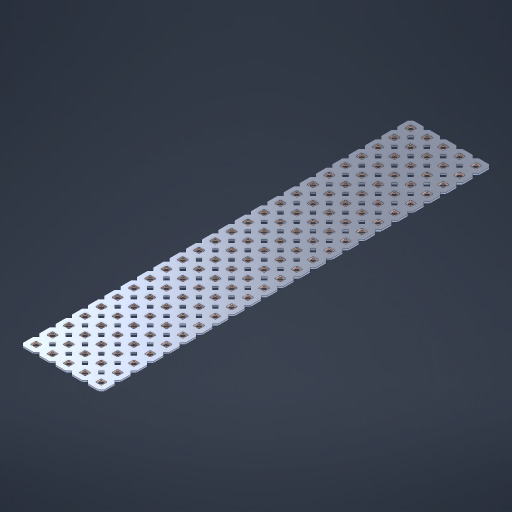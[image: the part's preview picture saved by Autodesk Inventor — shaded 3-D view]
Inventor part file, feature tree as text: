
AUTODESK INVENTOR PART (.ipt)
format: ipt  version: 2023 (Build 270158000, 158)  size: 1,647,616 bytes
history: native  units: in
note: dims shown in document units (in); Inventor stores cm internally (conversion verified against a paired STEP export)
features: other x121, extrude x119, sketch x2, pattern_linear x1
ambient origin geometry x8: Origin, YZ Plane, XZ Plane, XY Plane, X Axis, Y Axis, Z Axis, Center Point
bodies: Solid1 (feature_tree), Body (feature_tree)
feature tree (243):
  pattern_linear  "Rectangular Pattern1"  Spacing1=0.09in  [1 undecoded]
  sketch  "Sketch1"  dims[d1=0.5in]
  sketch  "Sketch2"  dims[d2=0.182in d3=0.09in d4=0.09in d5=0.09in d6=0.09in d7=0.09in d8=0.09in d9=0.09in d10=0.09in d11=0.02in d13=0.0in d14=0.172in d15=0.0625in d16=0.0in d19=0.5in d22=0.5in]
  other  "Srf1"
  other  "Srf126"
  other  "Srf127"
  other  "Srf128"
  other  "Srf129"
  other  "Srf130"
  other  "Srf131"
  other  "Srf250"
  other  "Srf251"
  other  "Srf252"
  other  "Srf253"
  other  "Srf254"
  other  "Srf255"
  other  "Srf256"
  other  "Srf257"
  other  "Srf258"
  other  "Srf259"
  other  "Srf260"
  other  "Srf261"
  other  "Srf262"
  other  "Srf263"
  other  "Srf264"
  other  "Srf265"
  other  "Srf266"
  other  "Srf268"
  other  "Srf269"
  other  "Srf270"
  other  "Srf271"
  other  "Srf272"
  other  "Srf273"
  other  "Srf274"
  other  "Srf275"
  other  "Srf276"
  other  "Srf277"
  other  "Srf278"
  other  "Srf279"
  other  "Srf280"
  other  "Srf281"
  other  "Srf282"
  other  "Srf283"
  other  "Srf284"
  other  "Srf285"
  other  "Srf286"
  other  "Srf287"
  other  "Srf288"
  other  "Srf289"
  other  "Srf290"
  other  "Srf291"
  other  "Srf293"
  other  "Srf294"
  other  "Srf295"
  other  "Srf296"
  other  "Srf297"
  other  "Srf298"
  other  "Srf299"
  other  "Srf300"
  other  "Srf301"
  other  "Srf302"
  other  "Srf303"
  other  "Srf304"
  other  "Srf305"
  other  "Srf306"
  other  "Srf307"
  other  "Srf308"
  other  "Srf309"
  other  "Srf310"
  other  "Srf311"
  other  "Srf312"
  other  "Srf313"
  other  "Srf314"
  other  "Srf315"
  other  "Srf316"
  other  "Srf318"
  other  "Srf319"
  other  "Srf320"
  other  "Srf321"
  other  "Srf322"
  other  "Srf323"
  other  "Srf324"
  other  "Srf325"
  other  "Srf326"
  other  "Srf327"
  other  "Srf328"
  other  "Srf329"
  other  "Srf330"
  other  "Srf331"
  other  "Srf332"
  other  "Srf333"
  other  "Srf334"
  other  "Srf335"
  other  "Srf336"
  other  "Srf337"
  other  "Srf338"
  other  "Srf339"
  other  "Srf340"
  other  "Srf341"
  other  "Srf343"
  other  "Srf344"
  other  "Srf345"
  other  "Srf346"
  other  "Srf347"
  other  "Srf348"
  other  "Srf349"
  other  "Srf350"
  other  "Srf351"
  other  "Srf352"
  other  "Srf353"
  other  "Srf354"
  other  "Srf355"
  other  "Srf356"
  other  "Srf357"
  other  "Srf358"
  other  "Srf359"
  other  "Srf360"
  other  "Srf361"
  other  "Srf362"
  other  "Srf363"
  other  "Srf364"
  other  "Srf365"
  other  "Srf366"
  other  "Circle"
  extrude  "ExtrusionSrf126"  Depth=0.09in
  extrude  "ExtrusionSrf127"  Depth=0.09in
  extrude  "ExtrusionSrf128"  Depth=0.09in
  extrude  "ExtrusionSrf129"  Depth=0.09in
  extrude  "ExtrusionSrf130"  Depth=0.09in
  extrude  "ExtrusionSrf131"  Depth=0.09in
  extrude  "ExtrusionSrf250"  Depth=0.09in
  extrude  "ExtrusionSrf251"  Depth=0.02in
  extrude  "ExtrusionSrf252"  TaperAngle=0.0deg  [1 undecoded]
  extrude  "ExtrusionSrf253"  Depth=0.5in
  extrude  "ExtrusionSrf254"  Depth=0.5in TaperAngle=0.0deg
  extrude  "ExtrusionSrf255"  Depth=0.5in
  extrude  "ExtrusionSrf256"  Depth=0.5in
  extrude  "ExtrusionSrf257"  [1 undecoded]
  extrude  "ExtrusionSrf258"  [1 undecoded]
  extrude  "ExtrusionSrf259"  [1 undecoded]
  extrude  "ExtrusionSrf260"  [1 undecoded]
  extrude  "ExtrusionSrf261"  [1 undecoded]
  extrude  "ExtrusionSrf262"  [1 undecoded]
  extrude  "ExtrusionSrf263"  [1 undecoded]
  extrude  "ExtrusionSrf264"  [1 undecoded]
  extrude  "ExtrusionSrf265"  [1 undecoded]
  extrude  "ExtrusionSrf266"  [1 undecoded]
  extrude  "ExtrusionSrf268"  [1 undecoded]
  extrude  "ExtrusionSrf269"  [1 undecoded]
  extrude  "ExtrusionSrf270"  [1 undecoded]
  extrude  "ExtrusionSrf271"  [1 undecoded]
  extrude  "ExtrusionSrf272"  [1 undecoded]
  extrude  "ExtrusionSrf273"  [1 undecoded]
  extrude  "ExtrusionSrf274"  [1 undecoded]
  extrude  "ExtrusionSrf275"  [1 undecoded]
  extrude  "ExtrusionSrf276"  [1 undecoded]
  extrude  "ExtrusionSrf277"  [1 undecoded]
  extrude  "ExtrusionSrf278"  [1 undecoded]
  extrude  "ExtrusionSrf279"  [1 undecoded]
  extrude  "ExtrusionSrf280"  [1 undecoded]
  extrude  "ExtrusionSrf281"  [1 undecoded]
  extrude  "ExtrusionSrf282"  [1 undecoded]
  extrude  "ExtrusionSrf283"  [1 undecoded]
  extrude  "ExtrusionSrf284"  [1 undecoded]
  extrude  "ExtrusionSrf285"  [1 undecoded]
  extrude  "ExtrusionSrf286"  [1 undecoded]
  extrude  "ExtrusionSrf287"  [1 undecoded]
  extrude  "ExtrusionSrf288"  [1 undecoded]
  extrude  "ExtrusionSrf289"  [1 undecoded]
  extrude  "ExtrusionSrf290"  [1 undecoded]
  extrude  "ExtrusionSrf291"  [1 undecoded]
  extrude  "ExtrusionSrf293"  [1 undecoded]
  extrude  "ExtrusionSrf294"  [1 undecoded]
  extrude  "ExtrusionSrf295"  [1 undecoded]
  extrude  "ExtrusionSrf296"  [1 undecoded]
  extrude  "ExtrusionSrf297"  [1 undecoded]
  extrude  "ExtrusionSrf298"  [1 undecoded]
  extrude  "ExtrusionSrf299"  [1 undecoded]
  extrude  "ExtrusionSrf300"  [1 undecoded]
  extrude  "ExtrusionSrf301"  [1 undecoded]
  extrude  "ExtrusionSrf302"  [1 undecoded]
  extrude  "ExtrusionSrf303"  [1 undecoded]
  extrude  "ExtrusionSrf304"  [1 undecoded]
  extrude  "ExtrusionSrf305"  [1 undecoded]
  extrude  "ExtrusionSrf306"  [1 undecoded]
  extrude  "ExtrusionSrf307"  [1 undecoded]
  extrude  "ExtrusionSrf308"  [1 undecoded]
  extrude  "ExtrusionSrf309"  [1 undecoded]
  extrude  "ExtrusionSrf310"  [1 undecoded]
  extrude  "ExtrusionSrf311"  [1 undecoded]
  extrude  "ExtrusionSrf312"  [1 undecoded]
  extrude  "ExtrusionSrf313"  [1 undecoded]
  extrude  "ExtrusionSrf314"  [1 undecoded]
  extrude  "ExtrusionSrf315"  [1 undecoded]
  extrude  "ExtrusionSrf316"  [1 undecoded]
  extrude  "ExtrusionSrf318"  [1 undecoded]
  extrude  "ExtrusionSrf319"  [1 undecoded]
  extrude  "ExtrusionSrf320"  [1 undecoded]
  extrude  "ExtrusionSrf321"  [1 undecoded]
  extrude  "ExtrusionSrf322"  [1 undecoded]
  extrude  "ExtrusionSrf323"  [1 undecoded]
  extrude  "ExtrusionSrf324"  [1 undecoded]
  extrude  "ExtrusionSrf325"  [1 undecoded]
  extrude  "ExtrusionSrf326"  [1 undecoded]
  extrude  "ExtrusionSrf327"  [1 undecoded]
  extrude  "ExtrusionSrf328"  [1 undecoded]
  extrude  "ExtrusionSrf329"  [1 undecoded]
  extrude  "ExtrusionSrf330"  [1 undecoded]
  extrude  "ExtrusionSrf331"  [1 undecoded]
  extrude  "ExtrusionSrf332"  [1 undecoded]
  extrude  "ExtrusionSrf333"  [1 undecoded]
  extrude  "ExtrusionSrf334"  [1 undecoded]
  extrude  "ExtrusionSrf335"  [1 undecoded]
  extrude  "ExtrusionSrf336"  [1 undecoded]
  extrude  "ExtrusionSrf337"  [1 undecoded]
  extrude  "ExtrusionSrf338"  [1 undecoded]
  extrude  "ExtrusionSrf339"  [1 undecoded]
  extrude  "ExtrusionSrf340"  [1 undecoded]
  extrude  "ExtrusionSrf341"  [1 undecoded]
  extrude  "ExtrusionSrf343"  [1 undecoded]
  extrude  "ExtrusionSrf344"  [1 undecoded]
  extrude  "ExtrusionSrf345"  [1 undecoded]
  extrude  "ExtrusionSrf346"  [1 undecoded]
  extrude  "ExtrusionSrf347"  [1 undecoded]
  extrude  "ExtrusionSrf348"  [1 undecoded]
  extrude  "ExtrusionSrf349"  [1 undecoded]
  extrude  "ExtrusionSrf350"  [1 undecoded]
  extrude  "ExtrusionSrf351"  [1 undecoded]
  extrude  "ExtrusionSrf352"  [1 undecoded]
  extrude  "ExtrusionSrf353"  [1 undecoded]
  extrude  "ExtrusionSrf354"  [1 undecoded]
  extrude  "ExtrusionSrf355"  [1 undecoded]
  extrude  "ExtrusionSrf356"  [1 undecoded]
  extrude  "ExtrusionSrf357"  [1 undecoded]
  extrude  "ExtrusionSrf358"  [1 undecoded]
  extrude  "ExtrusionSrf359"  [1 undecoded]
  extrude  "ExtrusionSrf360"  [1 undecoded]
  extrude  "ExtrusionSrf361"  [1 undecoded]
  extrude  "ExtrusionSrf362"  [1 undecoded]
  extrude  "ExtrusionSrf363"  [1 undecoded]
  extrude  "ExtrusionSrf364"  [1 undecoded]
  extrude  "ExtrusionSrf365"  [1 undecoded]
  extrude  "ExtrusionSrf366"  [1 undecoded]
note: 108 required parameter values undecoded (feature->parameter linkage not recoverable at this tier; creation-order binding heuristic only, values carry confidence <= 0.55)
